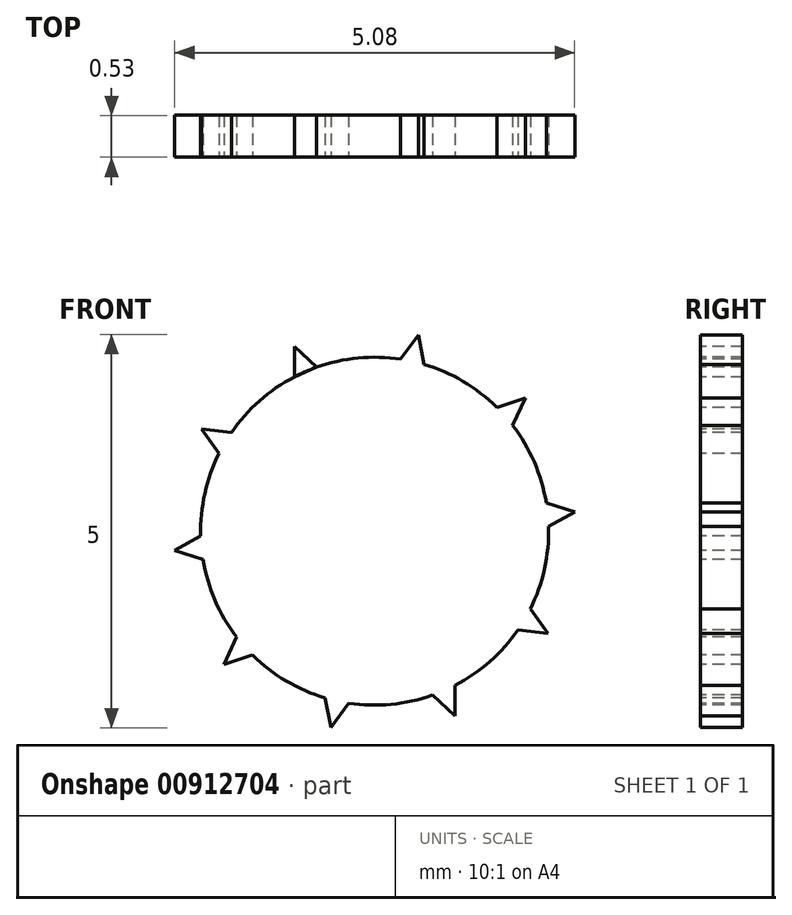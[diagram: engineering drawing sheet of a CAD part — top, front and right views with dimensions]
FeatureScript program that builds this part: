
annotation { "Feature Type Name" : "Feature", "Feature Type Description" : "" }
export const myFeature = defineFeature(function(context is Context, id is Id, definition is map)
    precondition{}
    {
        {
            var Q0;
            Q0=qCreatedBy(makeId("Front.planeOp"),FACE);
            var sketch = newSketch(context, id + "F0", { "sketchPlane" : qUnion([Q0])});
            skCircle(sketch, "E0", {"center": v(0, 0) * mm, "radius": 2.2 * mm});
            skLineSegment(sketch, "E1", {"start": v(-0.74, 2.08) * mm, "end": v(-1.02, 1.96) * mm});
            skLineSegment(sketch, "E2.MirrorCS", {"start": v(-1.02, 2.34) * mm, "end": v(-0.74, 2.08) * mm});
            skLineSegment(sketch, "E3.MirrorCS", {"start": v(-1.02, 1.96) * mm, "end": v(-1.02, 2.34) * mm});
            skLineSegment(sketch, "E4.1.0", {"start": v(-2.2, 1.3) * mm, "end": v(-1.82, 1.25) * mm});
            skLineSegment(sketch, "E4.1.1", {"start": v(-1.98, 0.99) * mm, "end": v(-2.2, 1.3) * mm});
            skLineSegment(sketch, "E4.2.0", {"start": v(-2.54, -0.24) * mm, "end": v(-2.2, -0.06) * mm});
            skLineSegment(sketch, "E4.2.1", {"start": v(-2.18, -0.36) * mm, "end": v(-2.54, -0.24) * mm});
            skLineSegment(sketch, "E4.3.0", {"start": v(-1.92, -1.7) * mm, "end": v(-1.75, -1.35) * mm});
            skLineSegment(sketch, "E4.3.1", {"start": v(-1.55, -1.57) * mm, "end": v(-1.92, -1.7) * mm});
            skLineSegment(sketch, "E4.4.0", {"start": v(-0.56, -2.5) * mm, "end": v(-0.63, -2.12) * mm});
            skLineSegment(sketch, "E4.4.1", {"start": v(-0.33, -2.19) * mm, "end": v(-0.56, -2.5) * mm});
            skLineSegment(sketch, "E4.5.0", {"start": v(1.02, -2.34) * mm, "end": v(0.74, -2.08) * mm});
            skLineSegment(sketch, "E4.5.1", {"start": v(1.02, -1.96) * mm, "end": v(1.02, -2.34) * mm});
            skLineSegment(sketch, "E4.6.0", {"start": v(2.2, -1.3) * mm, "end": v(1.82, -1.25) * mm});
            skLineSegment(sketch, "E4.6.1", {"start": v(1.98, -0.99) * mm, "end": v(2.2, -1.3) * mm});
            skLineSegment(sketch, "E4.7.0", {"start": v(2.54, 0.24) * mm, "end": v(2.2, 0.06) * mm});
            skLineSegment(sketch, "E4.7.1", {"start": v(2.18, 0.36) * mm, "end": v(2.54, 0.24) * mm});
            skLineSegment(sketch, "E4.8.0", {"start": v(1.92, 1.7) * mm, "end": v(1.75, 1.35) * mm});
            skLineSegment(sketch, "E4.8.1", {"start": v(1.55, 1.57) * mm, "end": v(1.92, 1.7) * mm});
            skLineSegment(sketch, "E4.9.0", {"start": v(0.56, 2.5) * mm, "end": v(0.63, 2.12) * mm});
            skLineSegment(sketch, "E4.9.1", {"start": v(0.33, 2.19) * mm, "end": v(0.56, 2.5) * mm});
            skSolve(sketch);
        }
        {
            var Q0;
            {var subQ5=sQuery(id+"F0.wireOp",EDGE,"E1");Q0=makeQuery(id+"F0.imprint","IMPRINT",FACE,{"disambiguationData":[TD([[makeQuery(id+"F0.imprint","IMPRINT",EDGE,{"derivedFrom":subQ5}),1.0]])]});}
            var Q1;
            {var subQ0=sQuery(id+"F0.wireOp",EDGE,"E4.9.0");Q1=makeQuery(id+"F0.imprint","IMPRINT",FACE,{"disambiguationData":[TD([[makeQuery(id+"F0.imprint","IMPRINT",EDGE,{"derivedFrom":subQ0}),-1.0]])]});}
            var Q2;
            {var subQ0=sQuery(id+"F0.wireOp",EDGE,"E4.8.0");Q2=makeQuery(id+"F0.imprint","IMPRINT",FACE,{"disambiguationData":[TD([[makeQuery(id+"F0.imprint","IMPRINT",EDGE,{"derivedFrom":subQ0}),-1.0]])]});}
            var Q3;
            {var subQ0=sQuery(id+"F0.wireOp",EDGE,"E4.7.0");Q3=makeQuery(id+"F0.imprint","IMPRINT",FACE,{"disambiguationData":[TD([[makeQuery(id+"F0.imprint","IMPRINT",EDGE,{"derivedFrom":subQ0}),-1.0]])]});}
            var Q4;
            {var subQ0=sQuery(id+"F0.wireOp",EDGE,"E4.6.0");Q4=makeQuery(id+"F0.imprint","IMPRINT",FACE,{"disambiguationData":[TD([[makeQuery(id+"F0.imprint","IMPRINT",EDGE,{"derivedFrom":subQ0}),-1.0]])]});}
            var Q5;
            {var subQ0=sQuery(id+"F0.wireOp",EDGE,"E4.5.0");Q5=makeQuery(id+"F0.imprint","IMPRINT",FACE,{"disambiguationData":[TD([[makeQuery(id+"F0.imprint","IMPRINT",EDGE,{"derivedFrom":subQ0}),-1.0]])]});}
            var Q6;
            {var subQ0=sQuery(id+"F0.wireOp",EDGE,"E4.4.0");Q6=makeQuery(id+"F0.imprint","IMPRINT",FACE,{"disambiguationData":[TD([[makeQuery(id+"F0.imprint","IMPRINT",EDGE,{"derivedFrom":subQ0}),-1.0]])]});}
            var Q7;
            {var subQ0=sQuery(id+"F0.wireOp",EDGE,"E4.3.0");Q7=makeQuery(id+"F0.imprint","IMPRINT",FACE,{"disambiguationData":[TD([[makeQuery(id+"F0.imprint","IMPRINT",EDGE,{"derivedFrom":subQ0}),-1.0]])]});}
            var Q8;
            {var subQ0=sQuery(id+"F0.wireOp",EDGE,"E4.2.0");Q8=makeQuery(id+"F0.imprint","IMPRINT",FACE,{"disambiguationData":[TD([[makeQuery(id+"F0.imprint","IMPRINT",EDGE,{"derivedFrom":subQ0}),-1.0]])]});}
            var Q9;
            {var subQ0=sQuery(id+"F0.wireOp",EDGE,"E4.1.0");Q9=makeQuery(id+"F0.imprint","IMPRINT",FACE,{"disambiguationData":[TD([[makeQuery(id+"F0.imprint","IMPRINT",EDGE,{"derivedFrom":subQ0}),-1.0]])]});}
            var Q10;
            {var subQ0=sQuery(id+"F0.wireOp",EDGE,"E2.MirrorCS");Q10=makeQuery(id+"F0.imprint","IMPRINT",FACE,{"disambiguationData":[TD([[makeQuery(id+"F0.imprint","IMPRINT",EDGE,{"derivedFrom":subQ0}),-1.0]])]});}
            extrude(context, id + "F1", {"entities" : qUnion([Q0, Q1, Q2, Q3, Q4, Q5, Q6, Q7, Q8, Q9, Q10]), "oppositeDirection" : true, "depth" : 0.53 * mm, "offsetDistance" : 25.4 * mm});
        }
    });
